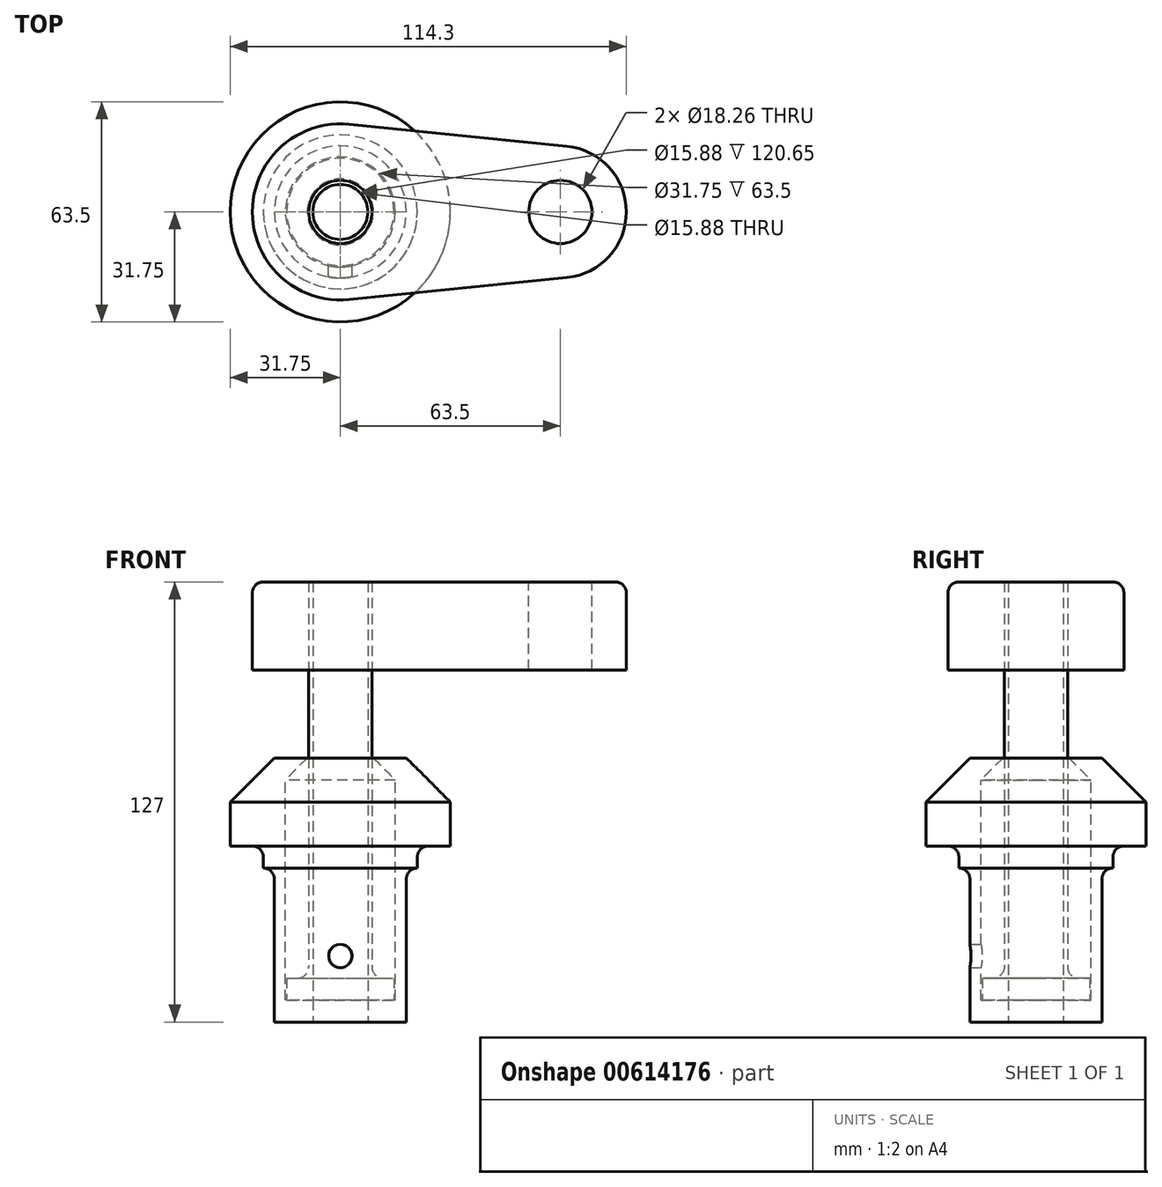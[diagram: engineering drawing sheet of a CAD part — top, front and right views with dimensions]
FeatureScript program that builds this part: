
annotation { "Feature Type Name" : "Feature", "Feature Type Description" : "" }
export const myFeature = defineFeature(function(context is Context, id is Id, definition is map)
    precondition{}
    {
        {
            var Q0;
            Q0=qCreatedBy(makeId("Front.planeOp"),FACE);
            var sketch = newSketch(context, id + "F0", { "sketchPlane" : qUnion([Q0])});
            skLineSegment(sketch, "E0", {"start": v(0, 0) * mm, "end": v(0, 76.2) * mm});
            skLineSegment(sketch, "E1", {"start": v(0, 76.2) * mm, "end": v(19.05, 76.2) * mm});
            skLineSegment(sketch, "E2", {"start": v(19.05, 76.2) * mm, "end": v(31.75, 63.5) * mm});
            skLineSegment(sketch, "E3", {"start": v(31.75, 63.5) * mm, "end": v(31.75, 50.8) * mm});
            skLineSegment(sketch, "E4", {"start": v(31.75, 50.8) * mm, "end": v(22.23, 50.8) * mm});
            skLineSegment(sketch, "E5", {"start": v(22.23, 50.8) * mm, "end": v(22.23, 44.45) * mm});
            skLineSegment(sketch, "E6", {"start": v(22.23, 44.45) * mm, "end": v(19.05, 44.45) * mm});
            skLineSegment(sketch, "E7", {"start": v(19.05, 44.45) * mm, "end": v(19.05, 0) * mm});
            skLineSegment(sketch, "E8", {"start": v(19.05, 0) * mm, "end": v(0, 0) * mm});
            skLineSegment(sketch, "E9", {"start": v(9.52, 76.2) * mm, "end": v(15.88, 69.85) * mm});
            skLineSegment(sketch, "E10", {"start": v(15.88, 69.85) * mm, "end": v(15.88, 6.35) * mm});
            skLineSegment(sketch, "E11", {"start": v(15.88, 6.35) * mm, "end": v(0, 6.35) * mm});
            skLineSegment(sketch, "E12", {"start": v(0, 76.2) * mm, "end": v(0, 94.4) * mm, "construction": true});
            skLineSegment(sketch, "E13", {"start": v(0, 76.2) * mm, "end": v(0, 127) * mm});
            skLineSegment(sketch, "E14", {"start": v(0, 127) * mm, "end": v(9.13, 127) * mm});
            skLineSegment(sketch, "E15", {"start": v(9.13, 127) * mm, "end": v(9.13, 12.7) * mm});
            skLineSegment(sketch, "E16", {"start": v(9.13, 12.7) * mm, "end": v(15.48, 12.7) * mm});
            skLineSegment(sketch, "E17", {"start": v(15.48, 12.7) * mm, "end": v(15.48, 6.35) * mm});
            skSolve(sketch);
        }
        {
            var Q0;
            {var subQ4=sQuery(id+"F0.wireOp",EDGE,"E2");Q0=makeQuery(id+"F0.imprint","IMPRINT",FACE,{"disambiguationData":[TD([[makeQuery(id+"F0.imprint","IMPRINT",EDGE,{"derivedFrom":subQ4}),-1.0]])]});}
            var Q1;
            Q1=sQuery(id+"F0.wireOp",EDGE,"E0");
            revolve(context, id + "F1", {"entities" : qUnion([Q0]), "axis" : qUnion([Q1]), "revolveType" : RevolveType.FULL, "oppositeDirection" : true});
        }
        {
            var Q0;
            {var subQ0=sQuery(id+"F0.wireOp",EDGE,"E13");Q0=makeQuery(id+"F0.imprint","IMPRINT",FACE,{"disambiguationData":[TD([[makeQuery(id+"F0.imprint","IMPRINT",EDGE,{"derivedFrom":subQ0}),-1.0]])]});}
            var Q1;
            {var subQ0=sQuery(id+"F0.wireOp",EDGE,"E16");Q1=makeQuery(id+"F0.imprint","IMPRINT",FACE,{"disambiguationData":[TD([[makeQuery(id+"F0.imprint","IMPRINT",EDGE,{"derivedFrom":subQ0}),-1.0]])]});}
            var Q2;
            Q2=sQuery(id+"F0.wireOp",EDGE,"E13");
            revolve(context, id + "F2", {"entities" : qUnion([Q0, Q1]), "axis" : qUnion([Q2]), "revolveType" : RevolveType.FULL});
        }
        {
            var Q0;
            Q0=makeQuery(id+"F2.opRevolve","SWEPT_FACE",FACE,{"disambiguationData":[OSD([sQuery(id+"F0.wireOp",EDGE,"E14")])]});
            var sketch = newSketch(context, id + "F3", { "sketchPlane" : qUnion([Q0])});
            skCircle(sketch, "E18", {"center": v(0, 0) * mm, "radius": 25.4 * mm});
            skCircle(sketch, "E19", {"center": v(63.5, 0) * mm, "radius": 19.05 * mm});
            skLineSegment(sketch, "E20", {"start": v(2.54, 25.27) * mm, "end": v(65.4, 18.95) * mm});
            skLineSegment(sketch, "E21", {"start": v(2.54, -25.27) * mm, "end": v(65.4, -18.95) * mm});
            skCircle(sketch, "E22.0", {"center": v(0, 0) * mm, "radius": 9.13 * mm});
            skCircle(sketch, "E23", {"center": v(63.5, 0) * mm, "radius": 9.13 * mm});
            skSolve(sketch);
        }
        {
            var Q0;
            Q0 = qSketchRegion(id + "F3", true);
            var Q1;
            Q1=makeQuery(id+"F1.opRevolve","SWEPT_FACE",FACE,{"disambiguationData":[OSD([sQuery(id+"F0.wireOp",EDGE,"E1")])]});
            extrude(context, id + "F4", {"entities" : qUnion([Q0]), "oppositeDirection" : true, "depth" : 25.4 * mm, "endBoundEntityFace" : qUnion([Q1]), "offsetDistance" : 1 / 812.8 * mm});
        }
        {
            var Q0;
            Q0=qCreatedBy(makeId("Front.planeOp"),FACE);
            var sketch = newSketch(context, id + "F5", { "sketchPlane" : qUnion([Q0])});
            skPoint(sketch, "E24", {"position": v(0, 19.05) * mm});
            skSolve(sketch);
        }
        {
            var Q0;
            Q0=sQuery(id+"F5.wireOp",VERTEX,"E24");
            var Q1;
            Q1=makeQuery(id+"F1.opRevolve","SWEPT_BODY",BODY,{"disambiguationData":[OSD([sQuery(id+"F0.wireOp",EDGE,"E0"),sQuery(id+"F0.wireOp",EDGE,"E1"),sQuery(id+"F0.wireOp",EDGE,"E2"),sQuery(id+"F0.wireOp",EDGE,"E3"),sQuery(id+"F0.wireOp",EDGE,"E4"),sQuery(id+"F0.wireOp",EDGE,"E5"),sQuery(id+"F0.wireOp",EDGE,"E6"),sQuery(id+"F0.wireOp",EDGE,"E7"),sQuery(id+"F0.wireOp",EDGE,"E8"),sQuery(id+"F0.wireOp",EDGE,"E9"),sQuery(id+"F0.wireOp",EDGE,"E10"),sQuery(id+"F0.wireOp",EDGE,"E11")])]});
            hole(context, id + "F6", {"style" : HoleStyle.SIMPLE, "endStyle" : HoleEndStyle.THROUGH, "oppositeDirection" : true, "standardTappedOrClearance" : lookupTablePath({ "standard" : "ANSI", "fit" : "Normal (ASME)", "size" : "1/4", "type" : "Clearance" }), "standardBlindInLast" : lookupTablePath({ "fit" : "Free", "standard" : "ANSI", "size" : "1/4", "type" : "Clearance" }), "holeDiameter" : 6.76 * mm, "majorDiameter" : 6.35 * mm, "tappedDepth" : 14.3 * mm, "tapClearance" : 3, "locations" : qUnion([Q0]), "scope" : qUnion([Q1])});
        }
        {
            var Q0;
            Q0=makeQuery(id+"F4.opExtrude","CAP_EDGE",EDGE,{"disambiguationData":[OSD([sQuery(id+"F3.wireOp",EDGE,"E20")])],"isStart":true});
            var Q1;
            Q1=makeQuery(id+"F1.opRevolve","SWEPT_EDGE",EDGE,{"disambiguationData":[OSD([sQuery(id+"F0.wireOp",EDGE,"E4"),sQuery(id+"F0.wireOp",EDGE,"E5")])]});
            var Q2;
            Q2=makeQuery(id+"F1.opRevolve","SWEPT_EDGE",EDGE,{"disambiguationData":[OSD([sQuery(id+"F0.wireOp",EDGE,"E6"),sQuery(id+"F0.wireOp",EDGE,"E7")])]});
            var Q3;
            Q3=makeQuery(id+"F2.opRevolve","SWEPT_EDGE",EDGE,{"disambiguationData":[OSD([sQuery(id+"F0.wireOp",EDGE,"E15"),sQuery(id+"F0.wireOp",EDGE,"E16")])]});
            fillet(context, id + "F7", {"entities" : qUnion([Q0, Q1, Q2, Q3]), "radius" : 3.17 * mm, "tangentPropagation" : true, "allowEdgeOverflow" : false});
        }
        {
            var Q0;
            Q0=makeQuery(id+"F1.opRevolve","SWEPT_FACE",FACE,{"disambiguationData":[OSD([sQuery(id+"F0.wireOp",EDGE,"E8")])]});
            var sketch = newSketch(context, id + "F8", { "sketchPlane" : qUnion([Q0])});
            skCircle(sketch, "E25", {"center": v(0, 0) * mm, "radius": 7.94 * mm});
            skSolve(sketch);
        }
        {
            var Q0;
            Q0 = qSketchRegion(id + "F8", true);
            extrude(context, id + "F9", {"entities" : qUnion([Q0]), "operationType" : NewBodyOperationType.REMOVE, "endBound" : BoundingType.THROUGH_ALL, "oppositeDirection" : true, "depth" : 25.4 * mm, "offsetDistance" : 25.4 * mm});
        }
    });
